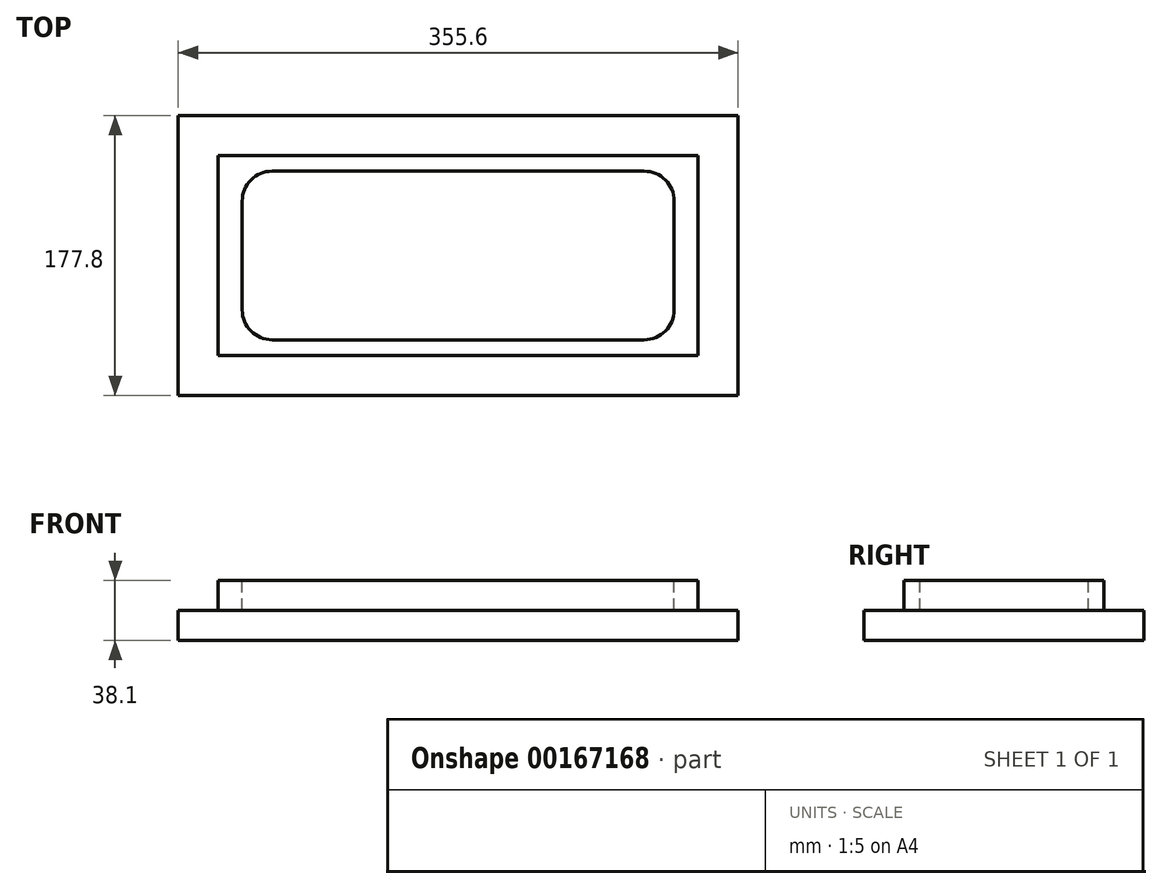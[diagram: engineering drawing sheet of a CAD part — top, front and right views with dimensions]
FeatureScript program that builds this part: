
annotation { "Feature Type Name" : "Feature", "Feature Type Description" : "" }
export const myFeature = defineFeature(function(context is Context, id is Id, definition is map)
    precondition{}
    {
        {
            var Q0;
            Q0=qCreatedBy(makeId("Top.planeOp"),FACE);
            var sketch = newSketch(context, id + "F0", { "sketchPlane" : qUnion([Q0])});
            skLineSegment(sketch, "E0.bottom", {"start": v(-177.8, 88.9) * mm, "end": v(177.8, 88.9) * mm});
            skLineSegment(sketch, "E0.top", {"start": v(-177.8, -88.9) * mm, "end": v(177.8, -88.9) * mm});
            skLineSegment(sketch, "E0.left", {"start": v(-177.8, 88.9) * mm, "end": v(-177.8, -88.9) * mm});
            skLineSegment(sketch, "E0.right", {"start": v(177.8, 88.9) * mm, "end": v(177.8, -88.9) * mm});
            skLineSegment(sketch, "E1", {"start": v(177.8, 88.9) * mm, "end": v(-177.8, -88.9) * mm, "construction": true});
            skSolve(sketch);
        }
        {
            var Q0;
            Q0 = qSketchRegion(id + "F0", true);
            extrude(context, id + "F1", {"entities" : qUnion([Q0]), "depth" : 19.05 * mm});
        }
        {
            var Q0;
            Q0=makeQuery(id+"F1.opExtrude","CAP_FACE",FACE,{"disambiguationData":[OSD([sQuery(id+"F0.wireOp",EDGE,"E0.bottom"),sQuery(id+"F0.wireOp",EDGE,"E0.top"),sQuery(id+"F0.wireOp",EDGE,"E0.left"),sQuery(id+"F0.wireOp",EDGE,"E0.right")])],"isStart":false});
            var sketch = newSketch(context, id + "F2", { "sketchPlane" : qUnion([Q0])});
            skLineSegment(sketch, "E2.bottom", {"start": v(-152.4, -63.5) * mm, "end": v(152.4, -63.5) * mm});
            skLineSegment(sketch, "E2.top", {"start": v(-152.4, 63.5) * mm, "end": v(152.4, 63.5) * mm});
            skLineSegment(sketch, "E2.left", {"start": v(-152.4, -63.5) * mm, "end": v(-152.4, 63.5) * mm});
            skLineSegment(sketch, "E2.right", {"start": v(152.4, -63.5) * mm, "end": v(152.4, 63.5) * mm});
            skSolve(sketch);
        }
        {
            var Q0;
            Q0=makeQuery(id+"F2.imprint","IMPRINT",FACE,{"disambiguationData":[TD([[makeQuery(id+"F2.imprint","IMPRINT",EDGE,{"derivedFrom":sQuery(id+"F2.wireOp",EDGE,"E2.bottom")}),1.0]])]});
            extrude(context, id + "F3", {"entities" : qUnion([Q0]), "operationType" : NewBodyOperationType.ADD, "depth" : 19.05 * mm});
        }
        {
            var Q0;
            Q0=makeQuery(id+"F3.opExtrude","CAP_FACE",FACE,{"disambiguationData":[OSD([sQuery(id+"F2.wireOp",EDGE,"E2.bottom"),sQuery(id+"F2.wireOp",EDGE,"E2.top"),sQuery(id+"F2.wireOp",EDGE,"E2.left"),sQuery(id+"F2.wireOp",EDGE,"E2.right")])],"isStart":false});
            var sketch = newSketch(context, id + "F4", { "sketchPlane" : qUnion([Q0])});
            skLineSegment(sketch, "E3.bottom", {"start": v(-118.11, -53.54) * mm, "end": v(118.11, -53.54) * mm});
            skLineSegment(sketch, "E3.top", {"start": v(-118.11, 53.54) * mm, "end": v(118.11, 53.54) * mm});
            skLineSegment(sketch, "E3.left", {"start": v(-137.16, -34.49) * mm, "end": v(-137.16, 34.49) * mm});
            skLineSegment(sketch, "E3.right", {"start": v(137.16, -34.49) * mm, "end": v(137.16, 34.49) * mm});
            skPoint(sketch, "E4.visualSharp", {"position": v(-137.16, -53.54) * mm});
            skArc(sketch, "E4.filletArc", {"start": v(-137.16, -34.49) * mm, "mid": v(-131.58, -47.96) * mm, "end": v(-118.11, -53.54) * mm});
            skPoint(sketch, "E5.visualSharp", {"position": v(-137.16, 53.54) * mm});
            skArc(sketch, "E5.filletArc", {"start": v(-118.11, 53.54) * mm, "mid": v(-131.58, 47.96) * mm, "end": v(-137.16, 34.49) * mm});
            skPoint(sketch, "E6.visualSharp", {"position": v(137.16, 53.54) * mm});
            skArc(sketch, "E6.filletArc", {"start": v(137.16, 34.49) * mm, "mid": v(131.58, 47.96) * mm, "end": v(118.11, 53.54) * mm});
            skPoint(sketch, "E7.visualSharp", {"position": v(137.16, -53.54) * mm});
            skArc(sketch, "E7.filletArc", {"start": v(118.11, -53.54) * mm, "mid": v(131.58, -47.96) * mm, "end": v(137.16, -34.49) * mm});
            skLineSegment(sketch, "E8", {"start": v(0, 63.5) * mm, "end": v(0, 53.54) * mm, "construction": true});
            skLineSegment(sketch, "E9", {"start": v(-152.4, 0) * mm, "end": v(-137.16, 0) * mm, "construction": true});
            skSolve(sketch);
        }
        {
            var Q0;
            Q0 = qSketchRegion(id + "F4", true);
            extrude(context, id + "F5", {"entities" : qUnion([Q0]), "operationType" : NewBodyOperationType.REMOVE, "oppositeDirection" : true, "depth" : 19.05 * mm});
        }
    });
